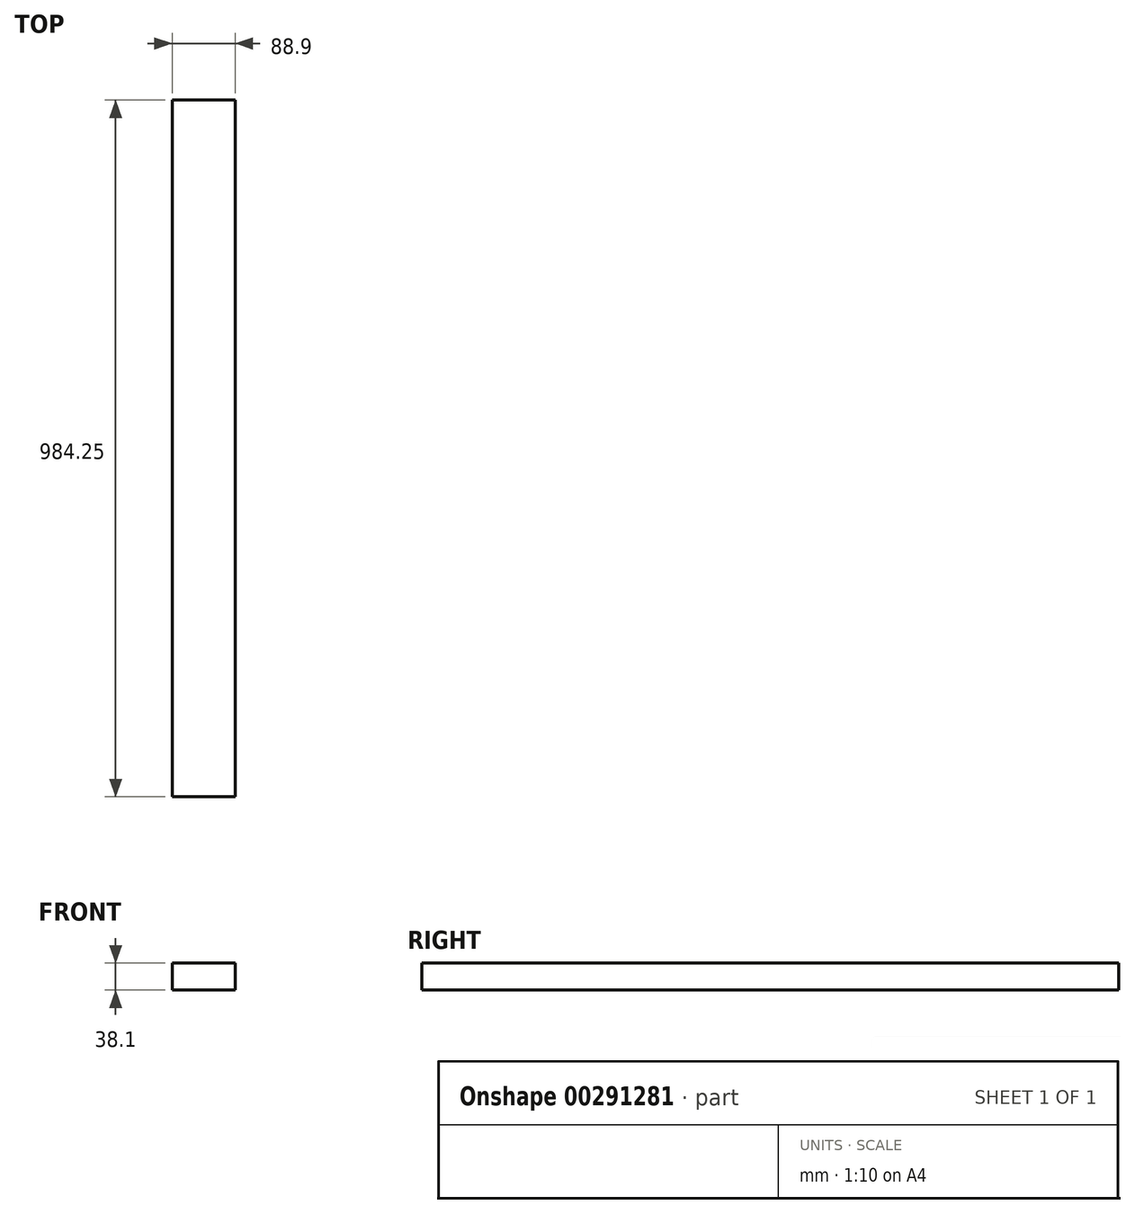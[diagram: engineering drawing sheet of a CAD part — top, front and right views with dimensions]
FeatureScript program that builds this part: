
annotation { "Feature Type Name" : "Feature", "Feature Type Description" : "" }
export const myFeature = defineFeature(function(context is Context, id is Id, definition is map)
    precondition{}
    {
        {
            var Q0;
            Q0=qCreatedBy(makeId("Front.planeOp"),FACE);
            var sketch = newSketch(context, id + "F0", { "sketchPlane" : qUnion([Q0])});
            skLineSegment(sketch, "E0", {"start": v(44.45, 19.05) * mm, "end": v(44.45, -19.05) * mm});
            skLineSegment(sketch, "E1", {"start": v(44.45, -19.05) * mm, "end": v(-44.45, -19.05) * mm});
            skLineSegment(sketch, "E2", {"start": v(-44.45, -19.05) * mm, "end": v(-44.45, 19.05) * mm});
            skLineSegment(sketch, "E3", {"start": v(-44.45, 19.05) * mm, "end": v(44.45, 19.05) * mm});
            skSolve(sketch);
        }
        {
            var Q0;
            Q0 = qSketchRegion(id + "F0", true);
            extrude(context, id + "F1", {"entities" : qUnion([Q0]), "depth" : 984.25 * mm});
        }
    });
